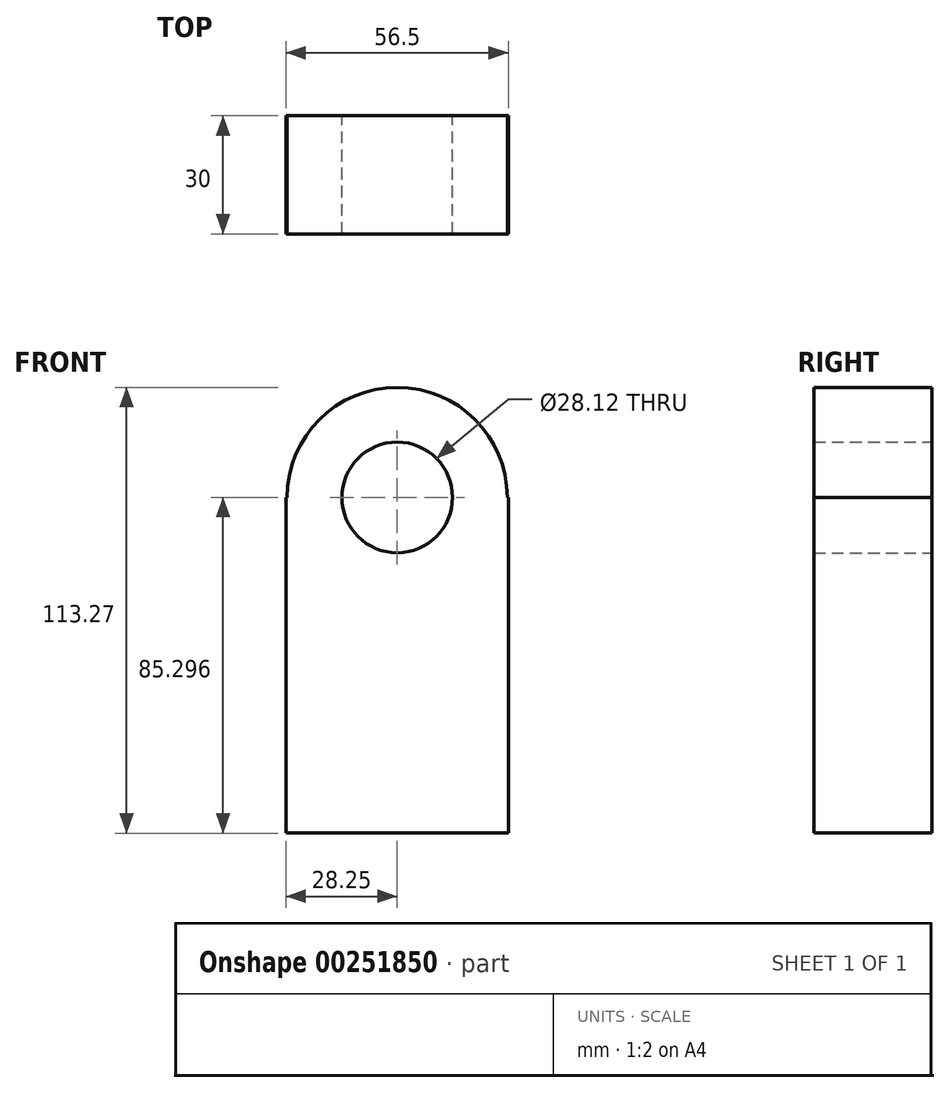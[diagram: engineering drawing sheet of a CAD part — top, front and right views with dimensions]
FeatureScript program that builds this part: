
annotation { "Feature Type Name" : "Feature", "Feature Type Description" : "" }
export const myFeature = defineFeature(function(context is Context, id is Id, definition is map)
    precondition{}
    {
        {
            var Q0;
            Q0=qCreatedBy(makeId("Front.planeOp"),FACE);
            var sketch = newSketch(context, id + "F0", { "sketchPlane" : qUnion([Q0])});
            skLineSegment(sketch, "E0.bottom", {"start": v(28.25, 42.65) * mm, "end": v(27.97, 42.65) * mm});
            skLineSegment(sketch, "E0.top", {"start": v(28.25, -42.65) * mm, "end": v(-28.25, -42.65) * mm});
            skLineSegment(sketch, "E0.left", {"start": v(28.25, 42.65) * mm, "end": v(28.25, -42.65) * mm});
            skLineSegment(sketch, "E0.right", {"start": v(-28.25, 42.65) * mm, "end": v(-28.25, -42.65) * mm});
            skPoint(sketch, "E0.middle", {"position": v(0, 0) * mm});
            skArc(sketch, "E1", {"start": v(27.97, 42.65) * mm, "mid": v(0, 70.62) * mm, "end": v(-27.97, 42.65) * mm});
            skCircle(sketch, "E2", {"center": v(0, 42.65) * mm, "radius": 14.06 * mm});
            skLineSegment(sketch, "E3.trimOffspring", {"start": v(-27.97, 42.65) * mm, "end": v(-28.25, 42.65) * mm});
            skSolve(sketch);
        }
        {
            var Q0;
            Q0=makeQuery(id+"F0.imprint","IMPRINT",FACE,{"disambiguationData":[TD([[makeQuery(id+"F0.imprint","IMPRINT",EDGE,{"derivedFrom":sQuery(id+"F0.wireOp",EDGE,"E0.bottom")}),1.0]])]});
            extrude(context, id + "F1", {"entities" : qUnion([Q0]), "depth" : 30 * mm});
        }
    });
